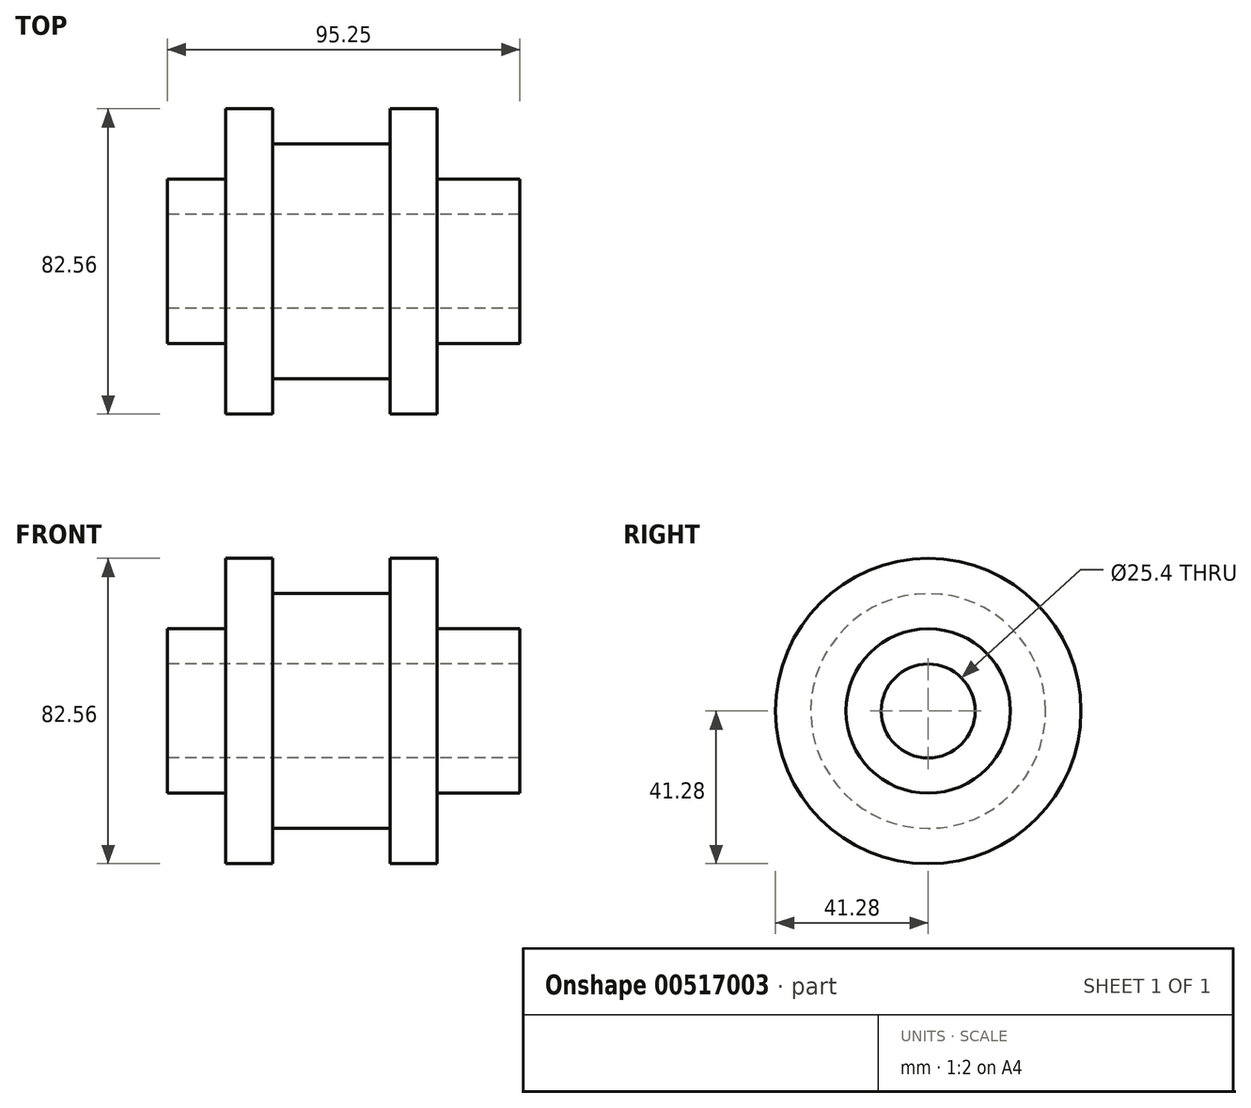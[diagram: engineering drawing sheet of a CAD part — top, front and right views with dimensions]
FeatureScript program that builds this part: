
annotation { "Feature Type Name" : "Feature", "Feature Type Description" : "" }
export const myFeature = defineFeature(function(context is Context, id is Id, definition is map)
    precondition{}
    {
        {
            var Q0;
            Q0=qCreatedBy(makeId("Front.planeOp"),FACE);
            var sketch = newSketch(context, id + "F0", { "sketchPlane" : qUnion([Q0])});
            skLineSegment(sketch, "E0", {"start": v(-70.18, 0) * mm, "end": v(70.18, 0) * mm, "construction": true});
            skPoint(sketch, "E1", {"position": v(0, 0) * mm});
            skLineSegment(sketch, "E2", {"start": v(-44.32, 12.7) * mm, "end": v(-44.32, 22.23) * mm});
            skLineSegment(sketch, "E3", {"start": v(-44.32, 22.23) * mm, "end": v(-28.58, 22.23) * mm});
            skLineSegment(sketch, "E4", {"start": v(-28.57, 22.23) * mm, "end": v(-28.58, 41.28) * mm});
            skLineSegment(sketch, "E5", {"start": v(-28.58, 41.27) * mm, "end": v(-15.88, 41.27) * mm});
            skLineSegment(sketch, "E6", {"start": v(-15.88, 41.27) * mm, "end": v(-15.88, 31.75) * mm});
            skLineSegment(sketch, "E7", {"start": v(-15.88, 31.75) * mm, "end": v(15.88, 31.75) * mm});
            skLineSegment(sketch, "E8", {"start": v(15.88, 31.75) * mm, "end": v(15.87, 41.28) * mm});
            skLineSegment(sketch, "E9", {"start": v(15.88, 41.28) * mm, "end": v(28.58, 41.28) * mm});
            skLineSegment(sketch, "E10", {"start": v(28.58, 41.28) * mm, "end": v(28.58, 22.23) * mm});
            skLineSegment(sketch, "E11", {"start": v(28.58, 22.23) * mm, "end": v(50.93, 22.23) * mm});
            skLineSegment(sketch, "E12", {"start": v(50.93, 22.23) * mm, "end": v(50.93, 12.7) * mm});
            skLineSegment(sketch, "E13", {"start": v(50.93, 12.7) * mm, "end": v(-44.32, 12.7) * mm});
            skPoint(sketch, "E14", {"position": v(0, 31.75) * mm});
            skSolve(sketch);
        }
        {
            var Q0;
            Q0=makeQuery(id+"F0.imprint","IMPRINT",FACE,{"disambiguationData":[TD([[makeQuery(id+"F0.imprint","IMPRINT",EDGE,{"derivedFrom":sQuery(id+"F0.wireOp",EDGE,"E2")}),-1.0]])]});
            var Q1;
            Q1=sQuery(id+"F0.wireOp",EDGE,"E0");
            revolve(context, id + "F1", {"entities" : qUnion([Q0]), "axis" : qUnion([Q1]), "revolveType" : RevolveType.FULL});
        }
    });
